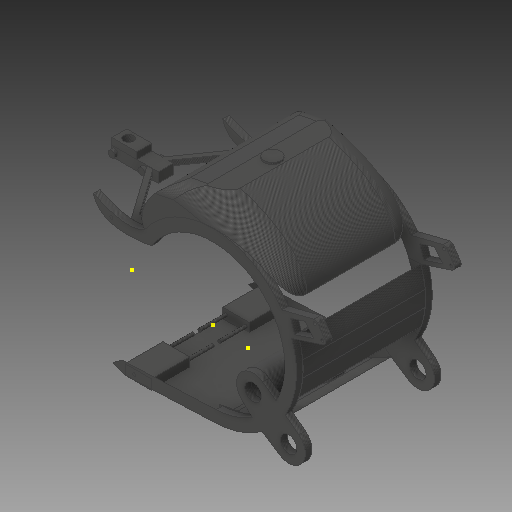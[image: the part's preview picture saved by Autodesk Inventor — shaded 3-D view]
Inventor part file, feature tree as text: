
AUTODESK INVENTOR PART (.ipt)
format: ipt  version: 2018 (Build 220112000, 112)  size: 759,808 bytes
history: native  units: mm
features: sketch x23, extrude x18, delete_face x11, mirror x9, fillet x5, plane x2, other x1
ambient origin geometry x8: Origin, YZ Plane, XZ Plane, XY Plane, X Axis, Y Axis, Z Axis, Center Point
bodies: Solid1 (feature_tree), Solid2 (feature_tree), Solid3 (feature_tree)
feature tree (69):
  other  "Main frame"
  extrude  "Extrusion1"  Depth=435.0mm
  plane  "Work Plane1"
  mirror  "Mirror1"
  extrude  "Extrusion2"  Depth=400.0mm
  delete_face  "Delete Face1"
  delete_face  "Delete Face2"
  extrude  "Extrusion3"  Depth=10.0mm
  extrude  "Extrusion4"  Depth=10.0mm
  mirror  "Mirror2"
  extrude  "Extrusion5"  Depth=50.0mm
  fillet  "Fillet1"  Radius=50.0mm
  fillet  "Fillet2"  Radius=100.0mm
  fillet  "Fillet3"  Radius=20.0mm
  fillet  "Fillet4"  Radius=185.0mm
  fillet  "Fillet5"  Radius=370.0mm
  extrude  "Extrusion6"  Depth=50.0mm
  extrude  "Extrusion7"  Depth=50.0mm
  mirror  "Mirror3"
  sketch  "Sketch8"  dims[d25=120.0mm d26=10.0mm]
  sketch  "Sketch9"  dims[d27=5.0mm d28=150.0mm d30=360.0deg]
  extrude  "Extrusion8"  Depth=10.0mm
  mirror  "Mirror4"
  extrude  "Extrusion9"  Depth=5.0mm TaperAngle=360.0deg
  extrude  "Extrusion10"  Depth=410.0mm TaperAngle=0.0deg
  mirror  "Mirror5"
  extrude  "Extrusion11"  Depth=2.0mm
  extrude  "Extrusion12"  Depth=65.5mm
  delete_face  "Delete Face3"
  mirror  "Mirror6"
  extrude  "Extrusion13"  Depth=50.0mm
  mirror  "Mirror7"
  sketch  "Sketch20"  dims[d48=40.607887mm d49=37.0mm]
  extrude  "Extrusion16"  Depth=5.0mm
  plane  "Work Plane3"
  mirror  "Mirror9"
  extrude  "Extrusion17"  Depth=115.0mm TaperAngle=0.0deg
  mirror  "Mirror10"
  extrude  "Extrusion18"  Depth=37.0mm
  delete_face  "Delete Face5"
  sketch  "Sketch24"  dims[d58=15.0mm d59=0.0mm]
  sketch  "Sketch25"  dims[d60=30.0mm]
  extrude  "Extrusion19"  Depth=25.0mm
  extrude  "Extrusion20"  Depth=45.0mm
  delete_face  "Delete Face6"
  delete_face  "Delete Face7"
  delete_face  "Delete Face8"
  delete_face  "Delete Face9"
  delete_face  "Delete Face10"
  delete_face  "Delete Face11"
  delete_face  "Delete Face12"
  sketch  "Sketch1"  dims[d0=505.0mm d1=435.0mm]
  sketch  "Sketch2"  dims[d2=400.0mm d4=64.0mm]
  sketch  "Sketch3"  dims[d5=100.0mm d8=10.0mm]
  sketch  "Sketch4"  dims[d9=10.0mm d10=100.0mm]
  sketch  "Sketch5"  dims[d11=100.0mm d12=50.0mm d13=50.0mm d14=100.0mm d15=20.0mm d16=0.0mm d17=185.0mm d18=370.0mm d19=0.0mm]
  sketch  "Sketch6"  dims[d20=100.0mm d21=50.0mm]
  sketch  "Sketch7"  dims[d22=165.0mm d23=0.0mm d24=50.0mm]
  sketch  "Sketch12"  dims[d32=40.0mm d33=0.0mm d34=410.0mm d35=0.0mm]
  sketch  "Sketch13"  dims[d36=40.5mm d37=2.0mm]
  sketch  "Sketch14"  dims[d38=42.1mm d39=65.5mm]
  sketch  "Sketch15"  dims[d40=77.6mm d41=50.0mm]
  sketch  "Sketch16"  dims[d42=5.0mm d43=0.0mm d44=80.0mm]
  sketch  "Sketch17"  dims[d45=30.0mm d46=115.0mm d47=0.0mm]
  sketch  "Sketch21"  dims[d50=25.0mm d51=0.0mm d52=170.0mm]
  sketch  "Sketch22"  dims[d54=140.0mm d55=45.0mm]
  sketch  "Sketch23"  dims[d56=30.0mm d57=0.0mm]
  sketch  "Sketch26"  dims[d61=5.0mm d62=0.0mm]
  sketch  "Sketch27"  dims[d63=30.0mm d64=10.0mm d65=80.0mm d66=0.0mm d67=10.0mm d70=10.0mm d71=0.0mm d78=20.0mm d79=90.0mm d80=20.0mm d81=10.0mm d82=0.0mm d83=10.0mm d84=10.0mm d85=0.0mm d86=370.0mm d87=0.0mm d90=20.0mm d91=0.0mm d92=20.0mm d93=0.0mm]
